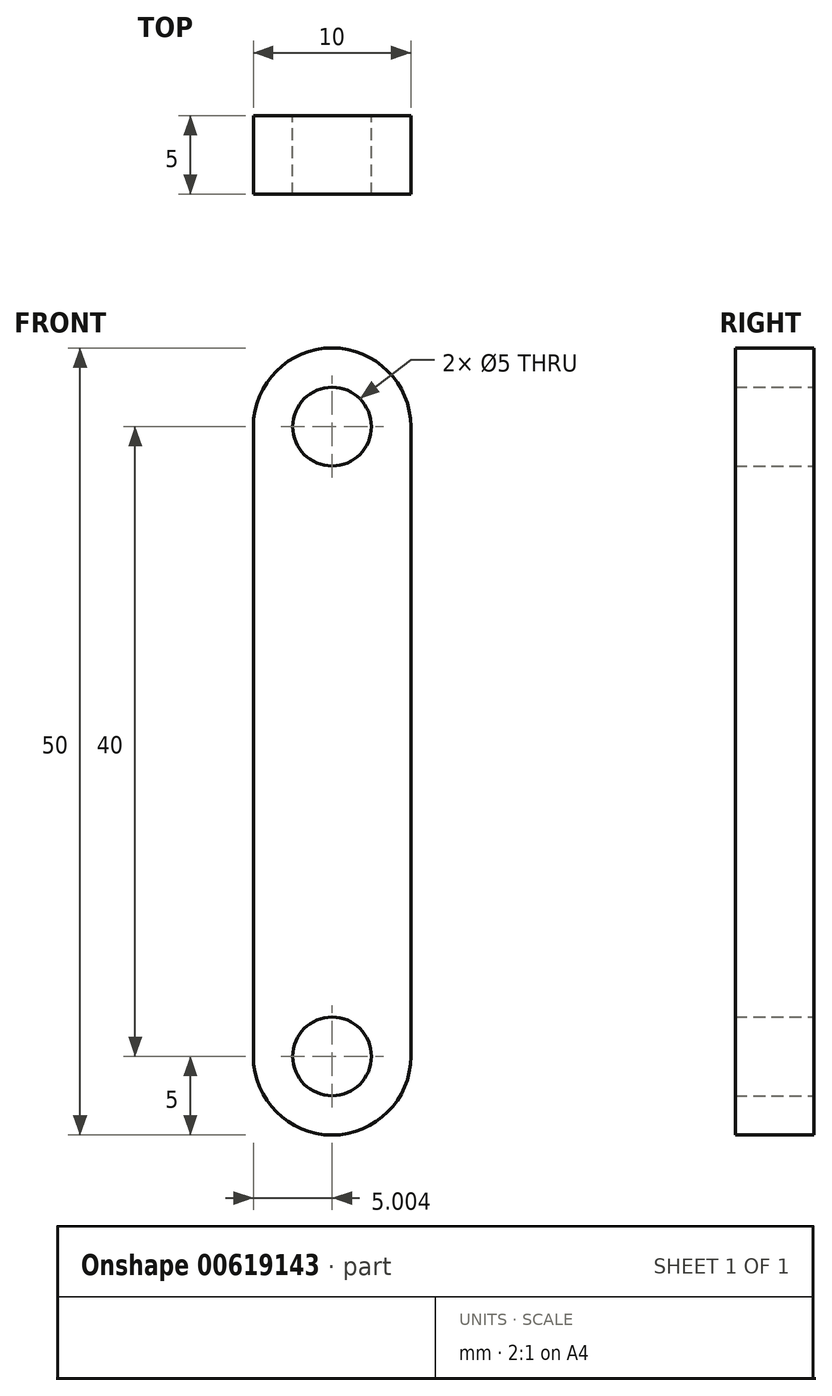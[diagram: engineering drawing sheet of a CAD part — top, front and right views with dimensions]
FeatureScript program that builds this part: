
annotation { "Feature Type Name" : "Feature", "Feature Type Description" : "" }
export const myFeature = defineFeature(function(context is Context, id is Id, definition is map)
    precondition{}
    {
        {
            var Q0;
            Q0=qCreatedBy(makeId("Front.planeOp"),FACE);
            var sketch = newSketch(context, id + "F0", { "sketchPlane" : qUnion([Q0])});
            skLineSegment(sketch, "E0", {"start": v(-16.85, 22.92) * mm, "end": v(-16.85, -17.08) * mm});
            skArc(sketch, "E1", {"start": v(-16.85, 22.92) * mm, "mid": v(-11.85, 27.92) * mm, "end": v(-6.85, 22.92) * mm});
            skLineSegment(sketch, "E2", {"start": v(-6.85, 22.92) * mm, "end": v(-6.85, -17.08) * mm});
            skArc(sketch, "E3", {"start": v(-16.85, -17.08) * mm, "mid": v(-11.85, -22.08) * mm, "end": v(-6.85, -17.08) * mm});
            skCircle(sketch, "E4", {"center": v(-11.85, 22.92) * mm, "radius": 2.5 * mm});
            skCircle(sketch, "E5", {"center": v(-11.85, -17.08) * mm, "radius": 2.5 * mm});
            skSolve(sketch);
        }
        {
            var Q0;
            Q0 = qSketchRegion(id + "F0", true);
            extrude(context, id + "F1", {"entities" : qUnion([Q0]), "depth" : 5 * mm, "offsetDistance" : 25 * mm});
        }
    });
